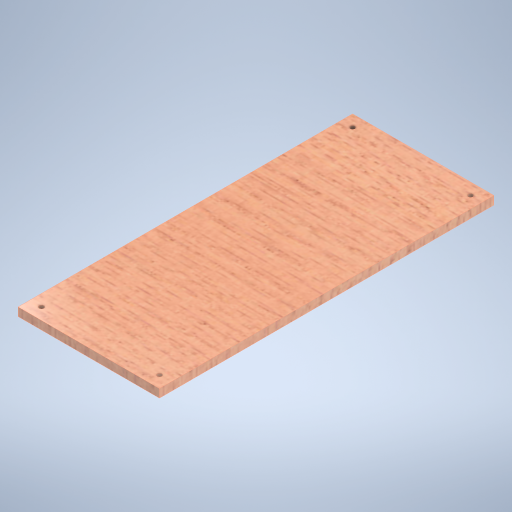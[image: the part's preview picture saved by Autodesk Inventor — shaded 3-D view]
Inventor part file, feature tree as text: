
AUTODESK INVENTOR PART (.ipt)
format: ipt  version: 2023.1 (Build 271208000, 208)  size: 358,400 bytes
history: native  units: in
note: dims shown in document units (in); Inventor stores cm internally (conversion verified against a paired STEP export)
features: extrude x2, sketch x2
ambient origin geometry x8: Origin, YZ Plane, XZ Plane, XY Plane, X Axis, Y Axis, Z Axis, Center Point
bodies: Solid1 (feature_tree)
feature tree (4):
  extrude  "Extrusion1"  Depth=0.1969in
  extrude  "Extrusion2"  Depth=0.1969in
  sketch  "Sketch1"  dims[d2=0.1969in d3=0.0in d4=0.1181in]
  sketch  "Sketch2"  dims[d5=0.1181in d6=0.1181in d7=0.1181in d8=0.2756in d9=0.2756in d10=0.2756in d11=0.2756in d12=0.2756in d13=0.2756in d14=0.2756in d15=0.2756in d16=0.1969in d17=0.0in]
